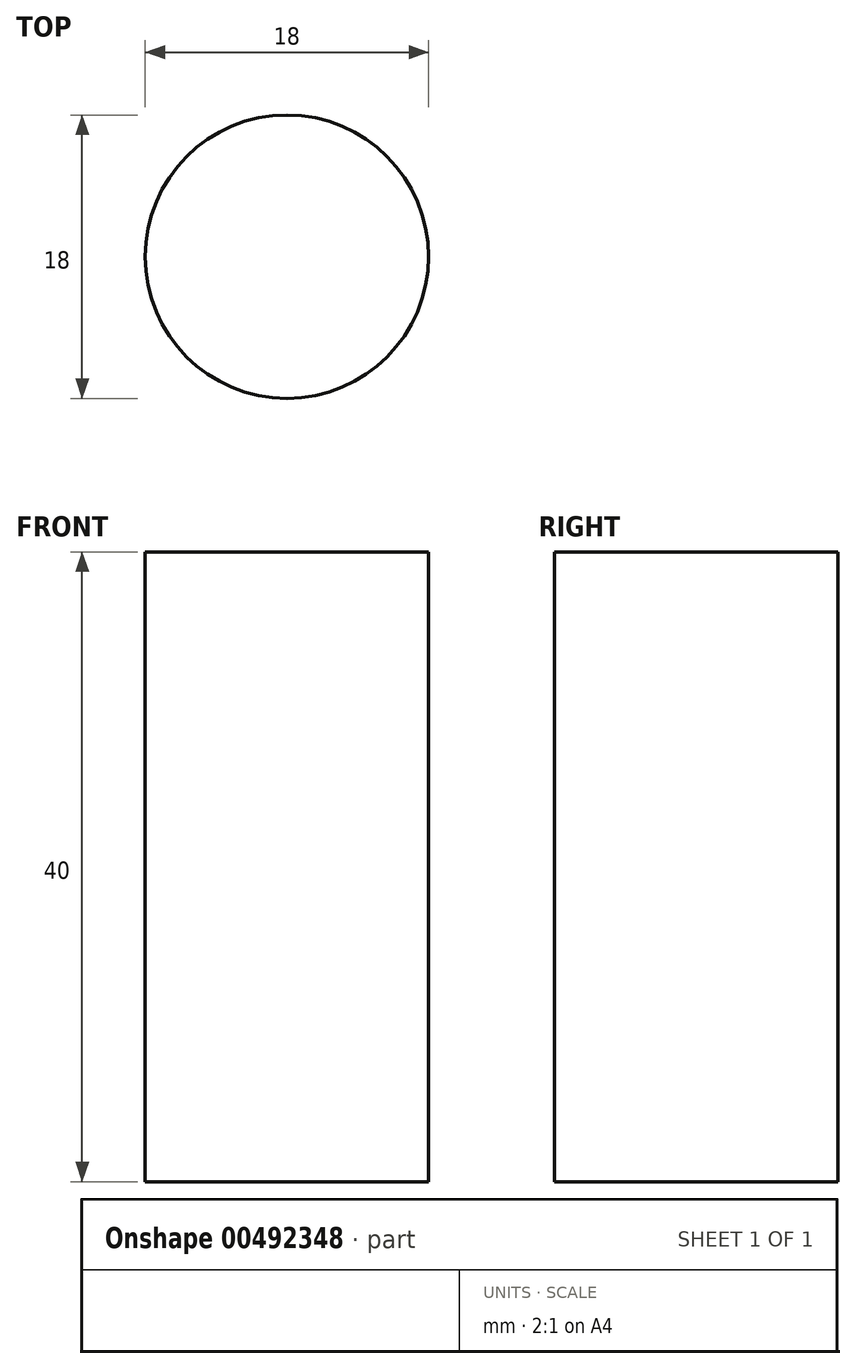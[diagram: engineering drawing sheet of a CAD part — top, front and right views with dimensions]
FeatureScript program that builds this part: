
annotation { "Feature Type Name" : "Feature", "Feature Type Description" : "" }
export const myFeature = defineFeature(function(context is Context, id is Id, definition is map)
    precondition{}
    {
        {
            var Q0;
            Q0=qCreatedBy(makeId("Top.planeOp"),FACE);
            var sketch = newSketch(context, id + "F0", { "sketchPlane" : qUnion([Q0])});
            skCircle(sketch, "E0", {"center": v(0, 0) * mm, "radius": 9 * mm});
            skSolve(sketch);
        }
        {
            var Q0;
            Q0=makeQuery(id+"F0.imprint","IMPRINT",FACE,{"disambiguationData":[TD([[makeQuery(id+"F0.imprint","IMPRINT",EDGE,{"derivedFrom":sQuery(id+"F0.wireOp",EDGE,"E0")}),1.0]])]});
            extrude(context, id + "F1", {"entities" : qUnion([Q0]), "depth" : 40 * mm});
        }
    });
